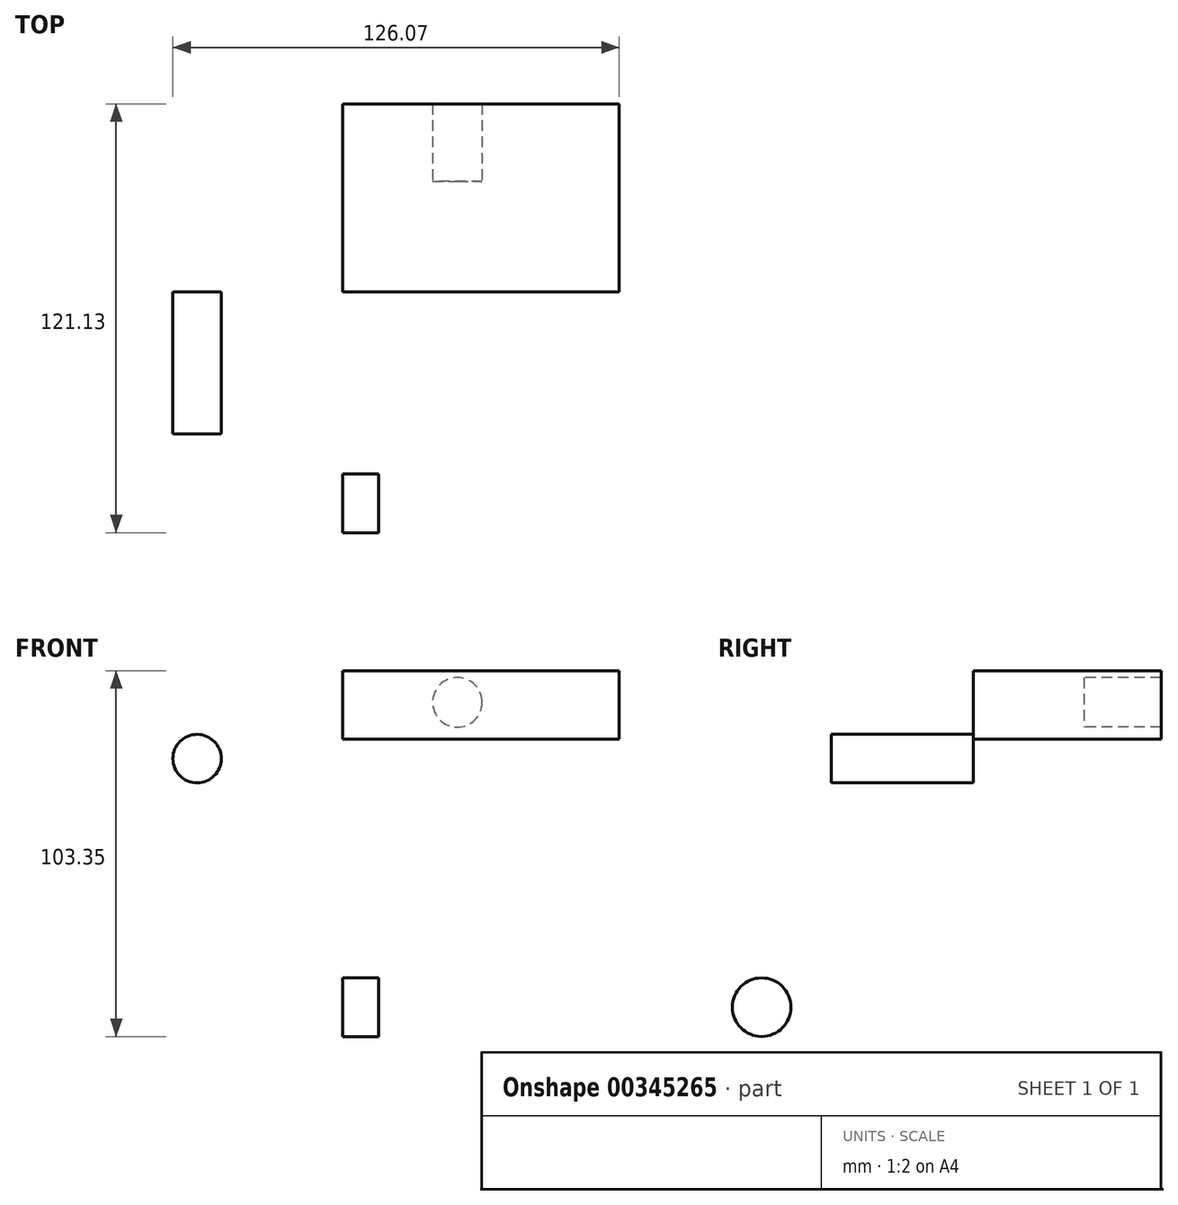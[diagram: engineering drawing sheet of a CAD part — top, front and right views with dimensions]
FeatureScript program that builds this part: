
annotation { "Feature Type Name" : "Feature", "Feature Type Description" : "" }
export const myFeature = defineFeature(function(context is Context, id is Id, definition is map)
    precondition{}
    {
        {
            var Q0;
            Q0=qCreatedBy(makeId("Front.planeOp"),FACE);
            var sketch = newSketch(context, id + "F0", { "sketchPlane" : qUnion([Q0])});
            skLineSegment(sketch, "E0.bottom", {"start": v(0, 0) * mm, "end": v(78.1, 0) * mm});
            skLineSegment(sketch, "E0.top", {"start": v(0, 19.34) * mm, "end": v(78.1, 19.34) * mm});
            skLineSegment(sketch, "E0.left", {"start": v(0, 0) * mm, "end": v(0, 19.34) * mm});
            skLineSegment(sketch, "E0.right", {"start": v(78.1, 0) * mm, "end": v(78.1, 19.34) * mm});
            skSolve(sketch);
        }
        {
            var Q0;
            Q0 = qSketchRegion(id + "F0", true);
            extrude(context, id + "F1", {"entities" : qUnion([Q0]), "oppositeDirection" : true, "depth" : 31.24 * mm});
        }
        {
            var Q0;
            Q0=qCreatedBy(makeId("Front.planeOp"),FACE);
            var sketch = newSketch(context, id + "F2", { "sketchPlane" : qUnion([Q0])});
            skCircle(sketch, "E1", {"center": v(-41.13, -5.48) * mm, "radius": 6.84 * mm});
            skSolve(sketch);
        }
        {
            var Q0;
            Q0 = qSketchRegion(id + "F2", true);
            extrude(context, id + "F3", {"entities" : qUnion([Q0]), "depth" : 40.13 * mm});
        }
        {
            var Q0;
            Q0=makeQuery(id+"F1.opExtrude","CAP_FACE",FACE,{"disambiguationData":[OSD([sQuery(id+"F0.wireOp",EDGE,"E0.bottom"),sQuery(id+"F0.wireOp",EDGE,"E0.top"),sQuery(id+"F0.wireOp",EDGE,"E0.left"),sQuery(id+"F0.wireOp",EDGE,"E0.right")])],"isStart":false});
            var sketch = newSketch(context, id + "F4", { "sketchPlane" : qUnion([Q0])});
            skCircle(sketch, "E2", {"center": v(-32.42, 10.43) * mm, "radius": 7 * mm});
            skSolve(sketch);
        }
        {
            var Q0;
            Q0=makeQuery(id+"F4.imprint","IMPRINT",FACE,{"disambiguationData":[TD([[makeQuery(id+"F4.imprint","IMPRINT",EDGE,{"derivedFrom":sQuery(id+"F4.wireOp",EDGE,"E2")}),-1.0]])]});
            extrude(context, id + "F5", {"entities" : qUnion([Q0]), "operationType" : NewBodyOperationType.ADD, "depth" : 21.84 * mm});
        }
        {
            var Q0;
            Q0=qCreatedBy(makeId("Right.planeOp"),FACE);
            var sketch = newSketch(context, id + "F6", { "sketchPlane" : qUnion([Q0])});
            skCircle(sketch, "E3", {"center": v(-59.76, -75.73) * mm, "radius": 8.28 * mm});
            skSolve(sketch);
        }
        {
            var Q0;
            Q0 = qSketchRegion(id + "F6", true);
            extrude(context, id + "F7", {"entities" : qUnion([Q0]), "depth" : 10.16 * mm});
        }
    });
